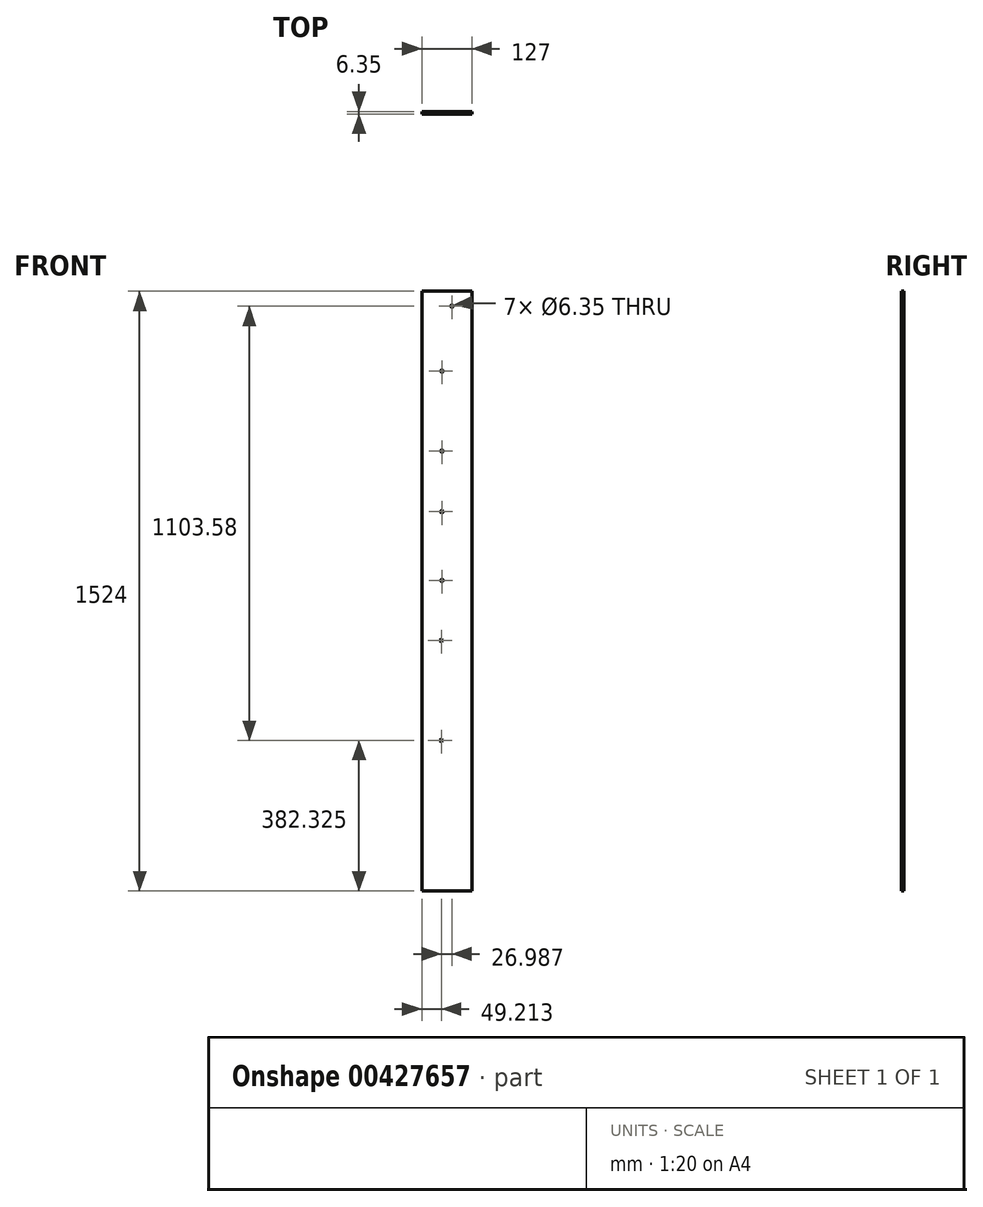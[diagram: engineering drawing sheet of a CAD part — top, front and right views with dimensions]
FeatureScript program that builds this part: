
annotation { "Feature Type Name" : "Feature", "Feature Type Description" : "" }
export const myFeature = defineFeature(function(context is Context, id is Id, definition is map)
    precondition{}
    {
        {
            var Q0;
            Q0=qCreatedBy(makeId("Front.planeOp"),FACE);
            var sketch = newSketch(context, id + "F0", { "sketchPlane" : qUnion([Q0])});
            skLineSegment(sketch, "E0.bottom", {"start": v(-117.55, 740.9) * mm, "end": v(9.45, 740.9) * mm});
            skLineSegment(sketch, "E0.top", {"start": v(-117.55, -783.1) * mm, "end": v(9.45, -783.1) * mm});
            skLineSegment(sketch, "E0.left", {"start": v(-117.55, 740.9) * mm, "end": v(-117.55, -783.1) * mm});
            skLineSegment(sketch, "E0.right", {"start": v(9.45, 740.9) * mm, "end": v(9.45, -783.1) * mm});
            skSolve(sketch);
        }
        {
            var Q0;
            Q0 = qSketchRegion(id + "F0", true);
            extrude(context, id + "F1", {"entities" : qUnion([Q0]), "depth" : 6.35 * mm});
        }
        {
            var Q0;
            Q0=makeQuery(id+"F1.opExtrude","CAP_FACE",FACE,{"disambiguationData":[OSD([sQuery(id+"F0.wireOp",EDGE,"E0.bottom"),sQuery(id+"F0.wireOp",EDGE,"E0.top"),sQuery(id+"F0.wireOp",EDGE,"E0.left"),sQuery(id+"F0.wireOp",EDGE,"E0.right")])],"isStart":false});
            var sketch = newSketch(context, id + "F2", { "sketchPlane" : qUnion([Q0])});
            skCircle(sketch, "E1", {"center": v(-41.35, 702.8) * mm, "radius": 1.59 * mm});
            skSolve(sketch);
        }
        {
            var Q0;
            Q0=sQuery(id+"F2.wireOp",VERTEX,"E1.center");
            var Q1;
            Q1=makeQuery(id+"F1.opExtrude","SWEPT_BODY",BODY,{"disambiguationData":[OSD([sQuery(id+"F0.wireOp",EDGE,"E0.bottom"),sQuery(id+"F0.wireOp",EDGE,"E0.top"),sQuery(id+"F0.wireOp",EDGE,"E0.left"),sQuery(id+"F0.wireOp",EDGE,"E0.right")])]});
            hole(context, id + "F3", {"style" : HoleStyle.SIMPLE, "endStyle" : HoleEndStyle.THROUGH, "holeDiameter" : 6.35 * mm, "isTappedThrough" : true, "tappedDepth" : 12.7 * mm, "tapClearance" : 3, "locations" : qUnion([Q0]), "scope" : qUnion([Q1])});
        }
        {
            var Q0;
            Q0=makeQuery(id+"F1.opExtrude","CAP_FACE",FACE,{"disambiguationData":[OSD([sQuery(id+"F0.wireOp",EDGE,"E0.bottom"),sQuery(id+"F0.wireOp",EDGE,"E0.top"),sQuery(id+"F0.wireOp",EDGE,"E0.left"),sQuery(id+"F0.wireOp",EDGE,"E0.right")])],"isStart":false});
            var sketch = newSketch(context, id + "F4", { "sketchPlane" : qUnion([Q0])});
            skCircle(sketch, "E2", {"center": v(-66.75, 537.7) * mm, "radius": 1.59 * mm});
            skSolve(sketch);
        }
        {
            var Q0;
            Q0=sQuery(id+"F4.wireOp",VERTEX,"E2.center");
            var Q1;
            Q1=makeQuery(id+"F1.opExtrude","SWEPT_BODY",BODY,{"disambiguationData":[OSD([sQuery(id+"F0.wireOp",EDGE,"E0.bottom"),sQuery(id+"F0.wireOp",EDGE,"E0.top"),sQuery(id+"F0.wireOp",EDGE,"E0.left"),sQuery(id+"F0.wireOp",EDGE,"E0.right")])]});
            hole(context, id + "F5", {"style" : HoleStyle.SIMPLE, "endStyle" : HoleEndStyle.THROUGH, "holeDiameter" : 6.35 * mm, "isTappedThrough" : true, "tappedDepth" : 12.7 * mm, "tapClearance" : 3, "locations" : qUnion([Q0]), "scope" : qUnion([Q1])});
        }
        {
            var Q0;
            Q0=makeQuery(id+"F1.opExtrude","CAP_FACE",FACE,{"disambiguationData":[OSD([sQuery(id+"F0.wireOp",EDGE,"E0.bottom"),sQuery(id+"F0.wireOp",EDGE,"E0.top"),sQuery(id+"F0.wireOp",EDGE,"E0.left"),sQuery(id+"F0.wireOp",EDGE,"E0.right")])],"isStart":false});
            var sketch = newSketch(context, id + "F6", { "sketchPlane" : qUnion([Q0])});
            skCircle(sketch, "E3", {"center": v(-66.75, 334.5) * mm, "radius": 1.59 * mm});
            skSolve(sketch);
        }
        {
            var Q0;
            Q0=sQuery(id+"F6.wireOp",VERTEX,"E3.center");
            var Q1;
            Q1=makeQuery(id+"F1.opExtrude","SWEPT_BODY",BODY,{"disambiguationData":[OSD([sQuery(id+"F0.wireOp",EDGE,"E0.bottom"),sQuery(id+"F0.wireOp",EDGE,"E0.top"),sQuery(id+"F0.wireOp",EDGE,"E0.left"),sQuery(id+"F0.wireOp",EDGE,"E0.right")])]});
            hole(context, id + "F7", {"style" : HoleStyle.SIMPLE, "endStyle" : HoleEndStyle.THROUGH, "holeDiameter" : 6.35 * mm, "isTappedThrough" : true, "tappedDepth" : 12.7 * mm, "tapClearance" : 3, "locations" : qUnion([Q0]), "scope" : qUnion([Q1])});
        }
        {
            var Q0;
            Q0=makeQuery(id+"F1.opExtrude","CAP_FACE",FACE,{"disambiguationData":[OSD([sQuery(id+"F0.wireOp",EDGE,"E0.bottom"),sQuery(id+"F0.wireOp",EDGE,"E0.top"),sQuery(id+"F0.wireOp",EDGE,"E0.left"),sQuery(id+"F0.wireOp",EDGE,"E0.right")])],"isStart":false});
            var sketch = newSketch(context, id + "F8", { "sketchPlane" : qUnion([Q0])});
            skCircle(sketch, "E4", {"center": v(-66.75, 180.5) * mm, "radius": 1.59 * mm});
            skSolve(sketch);
        }
        {
            var Q0;
            Q0=sQuery(id+"F8.wireOp",VERTEX,"E4.center");
            var Q1;
            Q1=makeQuery(id+"F1.opExtrude","SWEPT_BODY",BODY,{"disambiguationData":[OSD([sQuery(id+"F0.wireOp",EDGE,"E0.bottom"),sQuery(id+"F0.wireOp",EDGE,"E0.top"),sQuery(id+"F0.wireOp",EDGE,"E0.left"),sQuery(id+"F0.wireOp",EDGE,"E0.right")])]});
            hole(context, id + "F9", {"style" : HoleStyle.SIMPLE, "endStyle" : HoleEndStyle.THROUGH, "holeDiameter" : 6.35 * mm, "isTappedThrough" : true, "tappedDepth" : 12.7 * mm, "tapClearance" : 3, "locations" : qUnion([Q0]), "scope" : qUnion([Q1])});
        }
        {
            var Q0;
            Q0=makeQuery(id+"F1.opExtrude","CAP_FACE",FACE,{"disambiguationData":[OSD([sQuery(id+"F0.wireOp",EDGE,"E0.bottom"),sQuery(id+"F0.wireOp",EDGE,"E0.top"),sQuery(id+"F0.wireOp",EDGE,"E0.left"),sQuery(id+"F0.wireOp",EDGE,"E0.right")])],"isStart":false});
            var sketch = newSketch(context, id + "F10", { "sketchPlane" : qUnion([Q0])});
            skCircle(sketch, "E5", {"center": v(-66.75, 5.88) * mm, "radius": 1.59 * mm});
            skSolve(sketch);
        }
        {
            var Q0;
            Q0=sQuery(id+"F10.wireOp",VERTEX,"E5.center");
            var Q1;
            Q1=makeQuery(id+"F1.opExtrude","SWEPT_BODY",BODY,{"disambiguationData":[OSD([sQuery(id+"F0.wireOp",EDGE,"E0.bottom"),sQuery(id+"F0.wireOp",EDGE,"E0.top"),sQuery(id+"F0.wireOp",EDGE,"E0.left"),sQuery(id+"F0.wireOp",EDGE,"E0.right")])]});
            hole(context, id + "F11", {"style" : HoleStyle.SIMPLE, "endStyle" : HoleEndStyle.THROUGH, "holeDiameter" : 6.35 * mm, "isTappedThrough" : true, "tappedDepth" : 12.7 * mm, "tapClearance" : 3, "locations" : qUnion([Q0]), "scope" : qUnion([Q1])});
        }
        {
            var Q0;
            Q0=makeQuery(id+"F1.opExtrude","CAP_FACE",FACE,{"disambiguationData":[OSD([sQuery(id+"F0.wireOp",EDGE,"E0.bottom"),sQuery(id+"F0.wireOp",EDGE,"E0.top"),sQuery(id+"F0.wireOp",EDGE,"E0.left"),sQuery(id+"F0.wireOp",EDGE,"E0.right")])],"isStart":false});
            var sketch = newSketch(context, id + "F12", { "sketchPlane" : qUnion([Q0])});
            skCircle(sketch, "E6", {"center": v(-68.34, -146.68) * mm, "radius": 1.59 * mm});
            skSolve(sketch);
        }
        {
            var Q0;
            Q0=sQuery(id+"F12.wireOp",VERTEX,"E6.center");
            var Q1;
            Q1=makeQuery(id+"F1.opExtrude","SWEPT_BODY",BODY,{"disambiguationData":[OSD([sQuery(id+"F0.wireOp",EDGE,"E0.bottom"),sQuery(id+"F0.wireOp",EDGE,"E0.top"),sQuery(id+"F0.wireOp",EDGE,"E0.left"),sQuery(id+"F0.wireOp",EDGE,"E0.right")])]});
            hole(context, id + "F13", {"style" : HoleStyle.SIMPLE, "endStyle" : HoleEndStyle.THROUGH, "holeDiameter" : 6.35 * mm, "isTappedThrough" : true, "tappedDepth" : 12.7 * mm, "tapClearance" : 3, "locations" : qUnion([Q0]), "scope" : qUnion([Q1])});
        }
        {
            var Q0;
            Q0=makeQuery(id+"F1.opExtrude","CAP_FACE",FACE,{"disambiguationData":[OSD([sQuery(id+"F0.wireOp",EDGE,"E0.bottom"),sQuery(id+"F0.wireOp",EDGE,"E0.top"),sQuery(id+"F0.wireOp",EDGE,"E0.left"),sQuery(id+"F0.wireOp",EDGE,"E0.right")])],"isStart":false});
            var sketch = newSketch(context, id + "F14", { "sketchPlane" : qUnion([Q0])});
            skCircle(sketch, "E7", {"center": v(-68.34, -400.79) * mm, "radius": 1.59 * mm});
            skSolve(sketch);
        }
        {
            var Q0;
            Q0=sQuery(id+"F14.wireOp",VERTEX,"E7.center");
            var Q1;
            Q1=makeQuery(id+"F1.opExtrude","SWEPT_BODY",BODY,{"disambiguationData":[OSD([sQuery(id+"F0.wireOp",EDGE,"E0.bottom"),sQuery(id+"F0.wireOp",EDGE,"E0.top"),sQuery(id+"F0.wireOp",EDGE,"E0.left"),sQuery(id+"F0.wireOp",EDGE,"E0.right")])]});
            hole(context, id + "F15", {"style" : HoleStyle.SIMPLE, "endStyle" : HoleEndStyle.THROUGH, "holeDiameter" : 6.35 * mm, "isTappedThrough" : true, "tappedDepth" : 12.7 * mm, "tapClearance" : 3, "locations" : qUnion([Q0]), "scope" : qUnion([Q1])});
        }
    });
